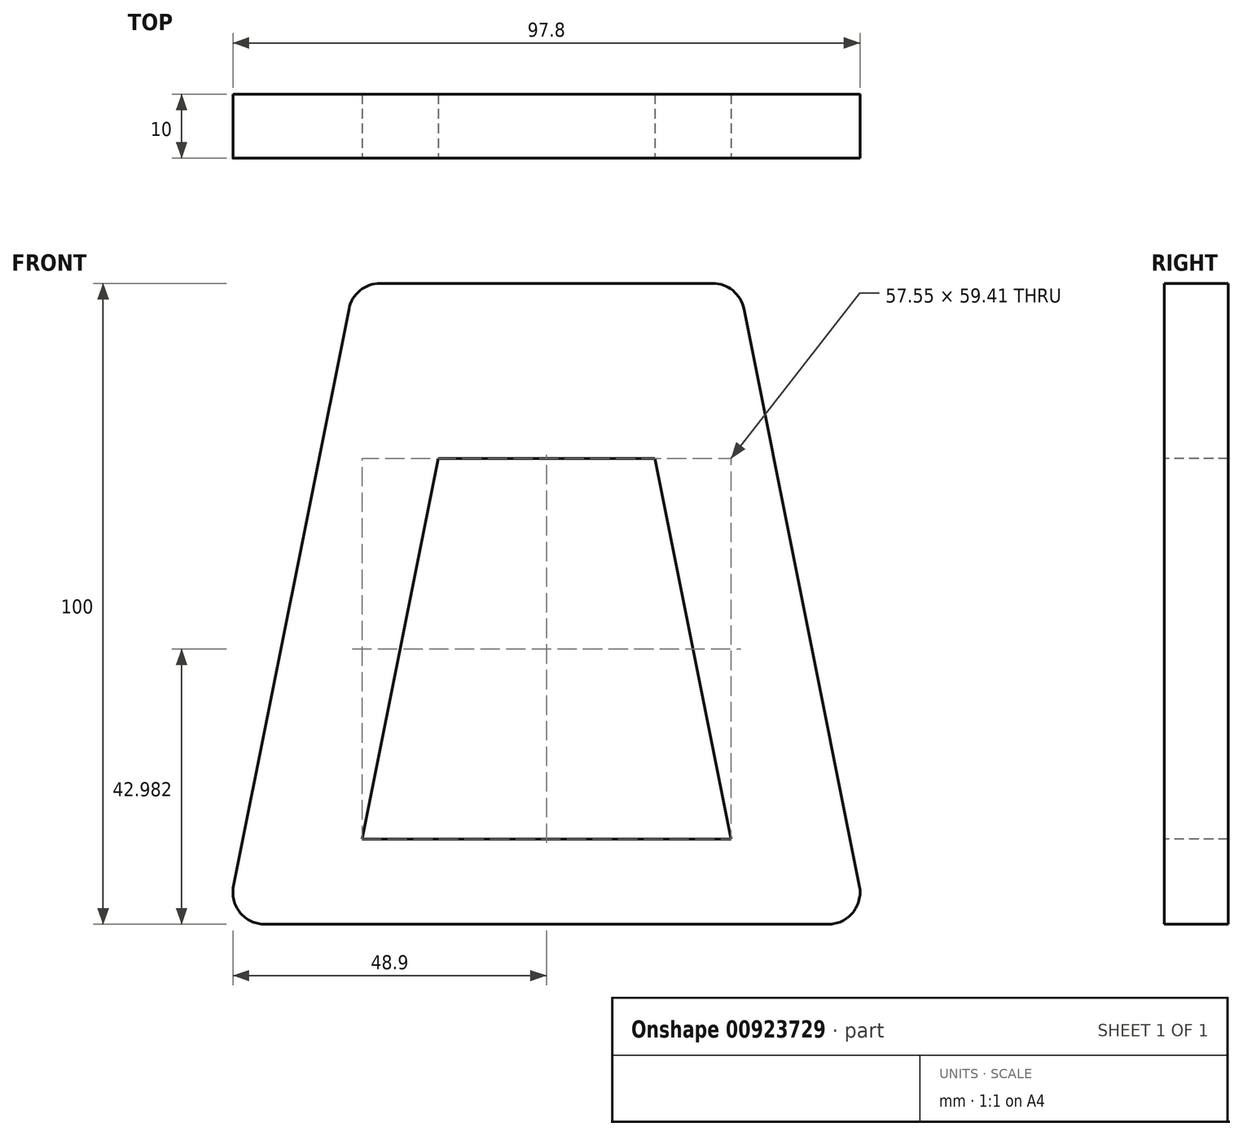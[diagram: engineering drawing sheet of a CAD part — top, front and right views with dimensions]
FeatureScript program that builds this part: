
annotation { "Feature Type Name" : "Feature", "Feature Type Description" : "" }
export const myFeature = defineFeature(function(context is Context, id is Id, definition is map)
    precondition{}
    {
        {
            var Q0;
            Q0=qCreatedBy(makeId("Front.planeOp"),FACE);
            var sketch = newSketch(context, id + "F0", { "sketchPlane" : qUnion([Q0])});
            skLineSegment(sketch, "E0", {"start": v(-50, 0) * mm, "end": v(50, 0) * mm});
            skLineSegment(sketch, "E1", {"start": v(50, 0) * mm, "end": v(30, 100) * mm});
            skLineSegment(sketch, "E2", {"start": v(30, 100) * mm, "end": v(-30, 100) * mm});
            skLineSegment(sketch, "E3", {"start": v(-30, 100) * mm, "end": v(-50, 0) * mm});
            skLineSegment(sketch, "E4", {"start": v(0, 0) * mm, "end": v(0, 100) * mm, "construction": true});
            skSolve(sketch);
        }
        {
            var Q0;
            Q0 = qSketchRegion(id + "F0", true);
            extrude(context, id + "F1", {"entities" : qUnion([Q0]), "depth" : 10 * mm, "offsetDistance" : 25 * mm});
        }
        {
            var Q0;
            Q0=makeQuery(id+"F1.opExtrude","SWEPT_EDGE",EDGE,{"disambiguationData":[OSD([sQuery(id+"F0.wireOp",EDGE,"E2"),sQuery(id+"F0.wireOp",EDGE,"E3")])]});
            var Q1;
            Q1=makeQuery(id+"F1.opExtrude","SWEPT_EDGE",EDGE,{"disambiguationData":[OSD([sQuery(id+"F0.wireOp",EDGE,"E1"),sQuery(id+"F0.wireOp",EDGE,"E2")])]});
            var Q2;
            Q2=makeQuery(id+"F1.opExtrude","SWEPT_EDGE",EDGE,{"disambiguationData":[OSD([sQuery(id+"F0.wireOp",EDGE,"E0"),sQuery(id+"F0.wireOp",EDGE,"E3")])]});
            var Q3;
            Q3=makeQuery(id+"F1.opExtrude","SWEPT_EDGE",EDGE,{"disambiguationData":[OSD([sQuery(id+"F0.wireOp",EDGE,"E0"),sQuery(id+"F0.wireOp",EDGE,"E1")])]});
            fillet(context, id + "F2", {"entities" : qUnion([Q0, Q1, Q2, Q3]), "radius" : 5 * mm, "tangentPropagation" : true, "allowEdgeOverflow" : false});
        }
        {
            var Q0;
            Q0=makeQuery(id+"F1.opExtrude","CAP_FACE",FACE,{"disambiguationData":[OSD([sQuery(id+"F0.wireOp",EDGE,"E0"),sQuery(id+"F0.wireOp",EDGE,"E1"),sQuery(id+"F0.wireOp",EDGE,"E2"),sQuery(id+"F0.wireOp",EDGE,"E3")])],"isStart":false});
            var sketch = newSketch(context, id + "F3", { "sketchPlane" : qUnion([Q0])});
            skLineSegment(sketch, "E5", {"start": v(-28.77, 13.28) * mm, "end": v(28.77, 13.28) * mm});
            skLineSegment(sketch, "E6", {"start": v(28.77, 13.28) * mm, "end": v(16.9, 72.69) * mm});
            skLineSegment(sketch, "E7", {"start": v(16.9, 72.69) * mm, "end": v(-16.9, 72.69) * mm});
            skLineSegment(sketch, "E8", {"start": v(-16.9, 72.69) * mm, "end": v(-28.77, 13.28) * mm});
            skLineSegment(sketch, "E9", {"start": v(0, 0) * mm, "end": v(0, 100) * mm, "construction": true});
            skSolve(sketch);
        }
        {
            var Q0;
            Q0 = qSketchRegion(id + "F3", true);
            extrude(context, id + "F4", {"entities" : qUnion([Q0]), "operationType" : NewBodyOperationType.REMOVE, "endBound" : BoundingType.THROUGH_ALL, "oppositeDirection" : true, "depth" : 5 * mm, "offsetDistance" : 25 * mm});
        }
    });
